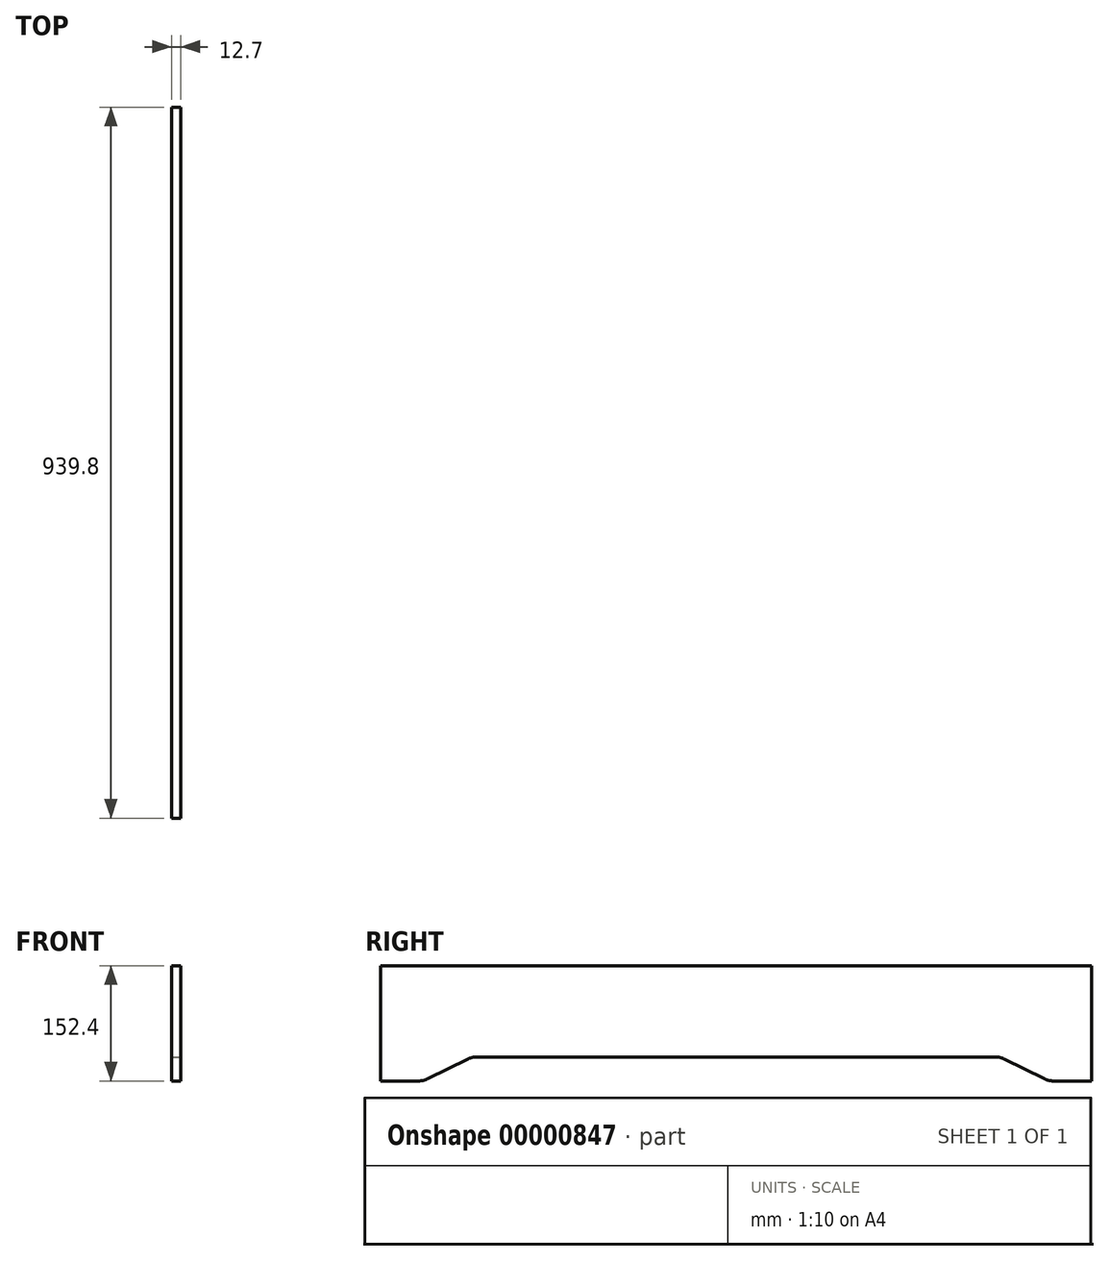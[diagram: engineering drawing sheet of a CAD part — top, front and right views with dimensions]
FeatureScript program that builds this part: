
annotation { "Feature Type Name" : "Feature", "Feature Type Description" : "" }
export const myFeature = defineFeature(function(context is Context, id is Id, definition is map)
    precondition{}
    {
        {
            var Q0;
            Q0=qCreatedBy(makeId("Right.planeOp"),FACE);
            var sketch = newSketch(context, id + "F0", { "sketchPlane" : qUnion([Q0])});
            skLineSegment(sketch, "E0.bottom", {"start": v(-469.9, 25.4) * mm, "end": v(0, 25.4) * mm});
            skLineSegment(sketch, "E0.top", {"start": v(-469.9, -127) * mm, "end": v(-419.1, -127) * mm});
            skLineSegment(sketch, "E0.left", {"start": v(-469.9, 25.4) * mm, "end": v(-469.9, -127) * mm});
            skLineSegment(sketch, "E0.right", {"start": v(0, 25.4) * mm, "end": v(0, -127) * mm});
            skLineSegment(sketch, "E1", {"start": v(-516.83, 0) * mm, "end": v(571.37, 0) * mm, "construction": true});
            skLineSegment(sketch, "E2", {"start": v(0, 121.88) * mm, "end": v(0, -242.75) * mm, "construction": true});
            skLineSegment(sketch, "E3", {"start": v(0, -95.25) * mm, "end": v(-342.9, -95.25) * mm});
            skArc(sketch, "E4.filletArc", {"start": v(-342.9, -95.25) * mm, "mid": v(-348.67, -95.91) * mm, "end": v(-354.14, -97.87) * mm});
            skPoint(sketch, "E5.newPointA", {"position": v(0, -127) * mm});
            skArc(sketch, "E5.filletArc", {"start": v(-419.1, -127) * mm, "mid": v(-413.33, -126.34) * mm, "end": v(-407.86, -124.38) * mm});
            skLineSegment(sketch, "E6", {"start": v(-407.86, -124.38) * mm, "end": v(-354.14, -97.87) * mm});
            skSolve(sketch);
        }
        {
            var Q0;
            Q0 = qSketchRegion(id + "F0", true);
            extrude(context, id + "F1", {"entities" : qUnion([Q0]), "oppositeDirection" : true, "depth" : 12.7 * mm});
        }
        {
            var Q0;
            Q0=makeQuery(id+"F1.opExtrude","SWEPT_BODY",BODY,{"disambiguationData":[OSD([sQuery(id+"F0.wireOp",EDGE,"E0.bottom"),sQuery(id+"F0.wireOp",EDGE,"E0.top"),sQuery(id+"F0.wireOp",EDGE,"E0.left"),sQuery(id+"F0.wireOp",EDGE,"E0.right")])]});
            var Q1;
            Q1=makeQuery(id+"F1.opExtrude","SWEPT_FACE",FACE,{"disambiguationData":[OSD([sQuery(id+"F0.wireOp",EDGE,"E0.right")])]});
            mirror(context, id + "F2", {"operationType" : NewBodyOperationType.ADD, "entities" : qUnion([Q0]), "mirrorPlane" : qUnion([Q1])});
        }
    });
